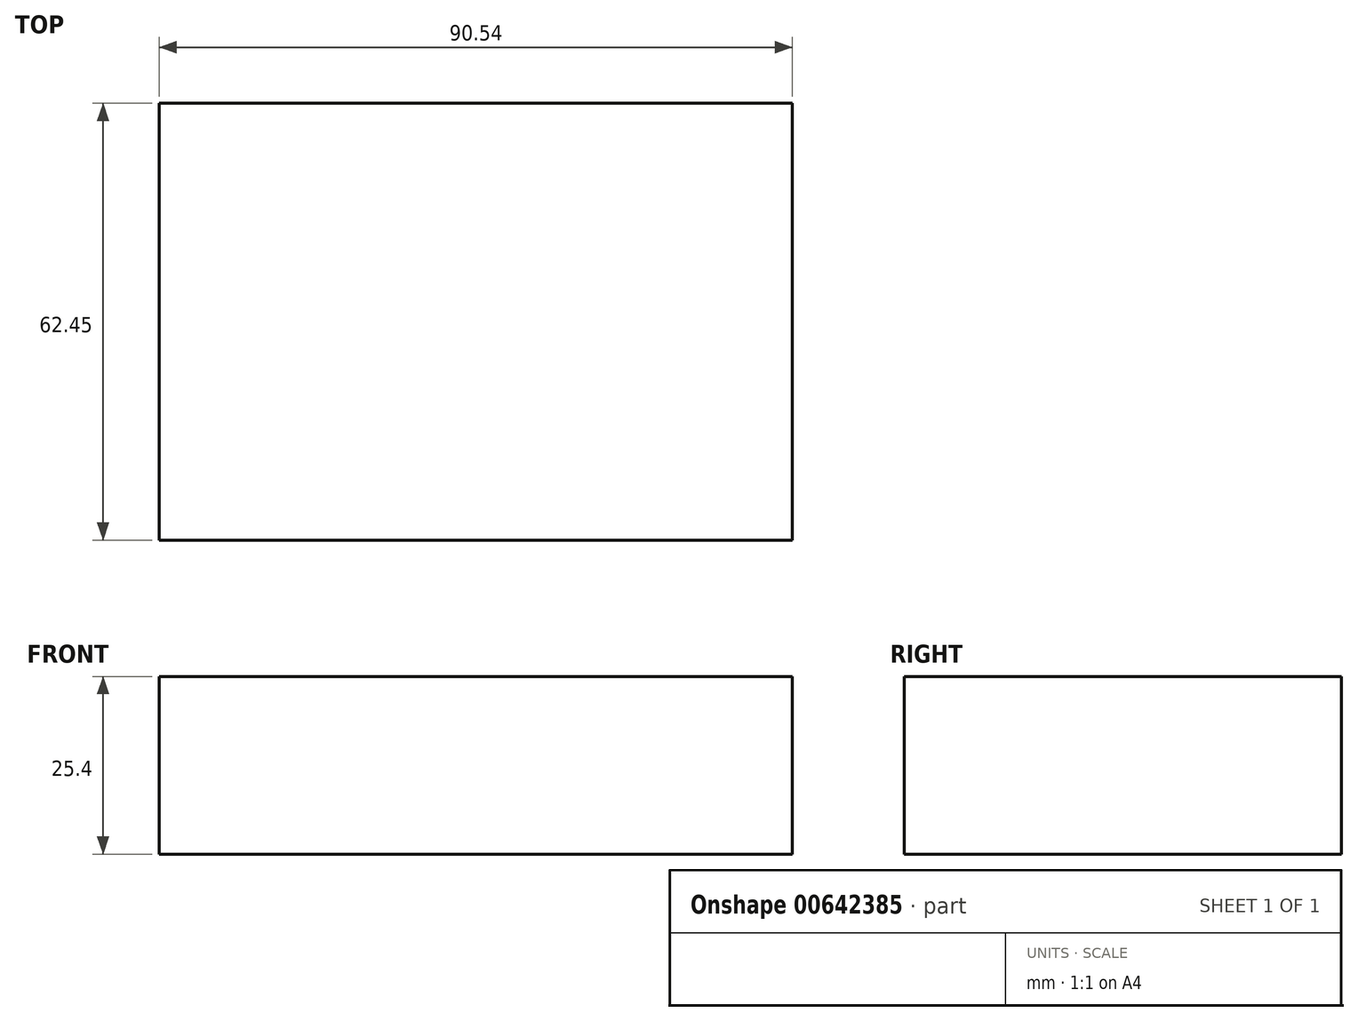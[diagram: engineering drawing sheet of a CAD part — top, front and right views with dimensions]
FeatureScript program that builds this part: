
annotation { "Feature Type Name" : "Feature", "Feature Type Description" : "" }
export const myFeature = defineFeature(function(context is Context, id is Id, definition is map)
    precondition{}
    {
        {
            var Q0;
            Q0=qCreatedBy(makeId("Top.planeOp"),FACE);
            var sketch = newSketch(context, id + "F0", { "sketchPlane" : qUnion([Q0])});
            skLineSegment(sketch, "E0.bottom", {"start": v(-62.07, -4) * mm, "end": v(28.47, -4) * mm});
            skLineSegment(sketch, "E0.top", {"start": v(-62.07, -66.45) * mm, "end": v(28.47, -66.45) * mm});
            skLineSegment(sketch, "E0.left", {"start": v(-62.07, -4) * mm, "end": v(-62.07, -66.45) * mm});
            skLineSegment(sketch, "E0.right", {"start": v(28.47, -4) * mm, "end": v(28.47, -66.45) * mm});
            skSolve(sketch);
        }
        {
            var Q0;
            Q0=makeQuery(id+"F0.imprint","IMPRINT",FACE,{"disambiguationData":[TD([[makeQuery(id+"F0.imprint","IMPRINT",EDGE,{"derivedFrom":sQuery(id+"F0.wireOp",EDGE,"E0.bottom")}),-1.0]])]});
            extrude(context, id + "F1", {"entities" : qUnion([Q0]), "depth" : 25.4 * mm, "offsetDistance" : 25.4 * mm});
        }
    });
